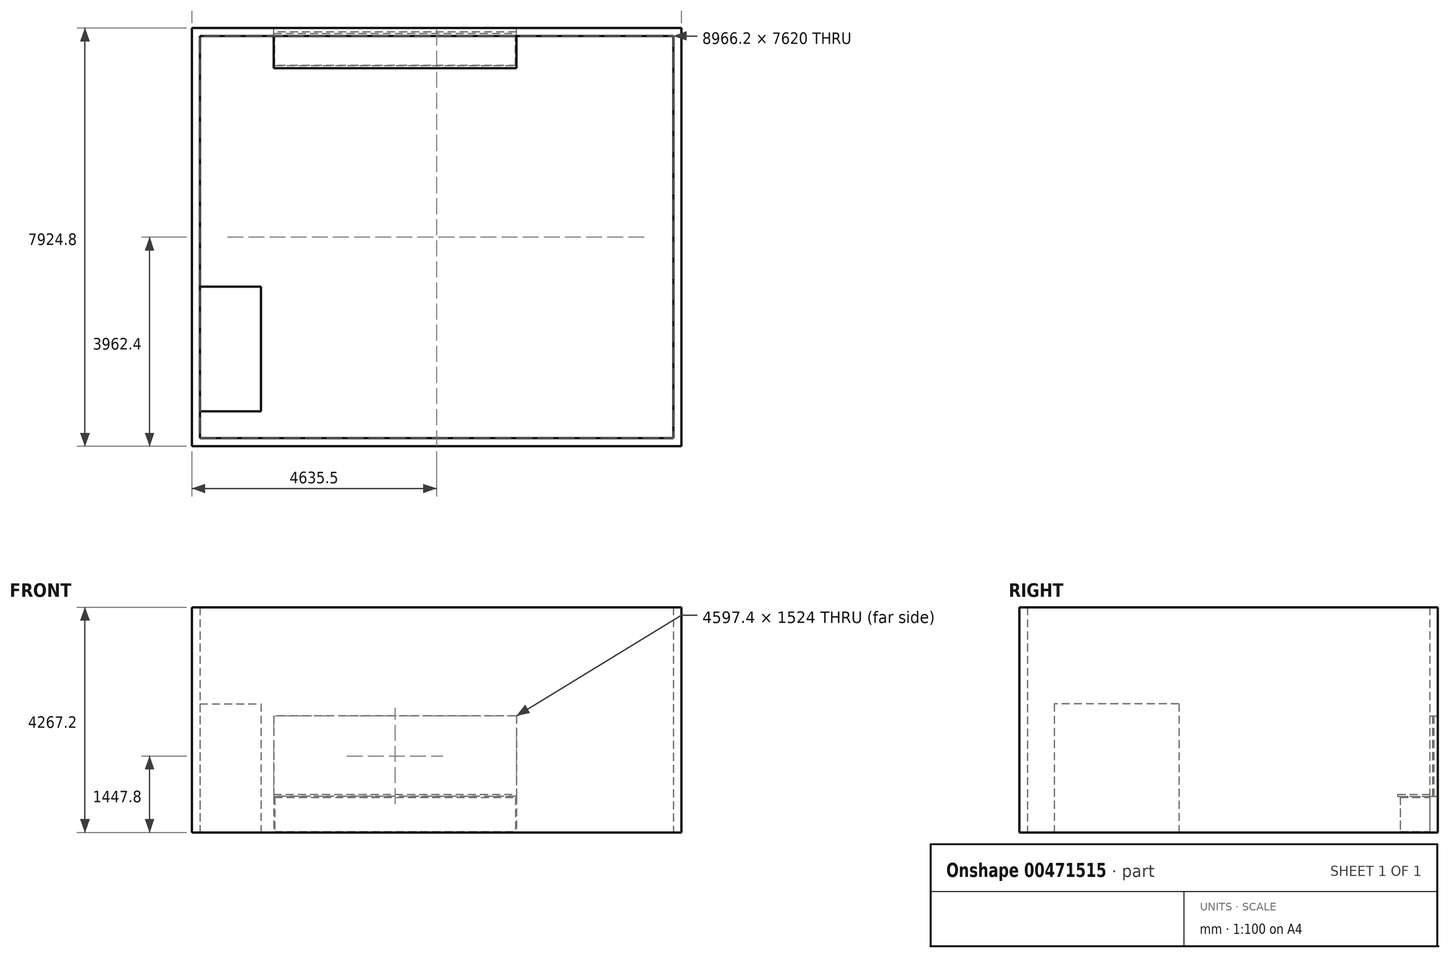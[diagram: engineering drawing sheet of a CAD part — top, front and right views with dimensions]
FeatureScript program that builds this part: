
annotation { "Feature Type Name" : "Feature", "Feature Type Description" : "" }
export const myFeature = defineFeature(function(context is Context, id is Id, definition is map)
    precondition{}
    {
        {
            var Q0;
            Q0=qCreatedBy(makeId("Top.planeOp"),FACE);
            var sketch = newSketch(context, id + "F0", { "sketchPlane" : qUnion([Q0])});
            skLineSegment(sketch, "E0.bottom", {"start": v(4483.1, -3810) * mm, "end": v(-4483.1, -3810) * mm});
            skLineSegment(sketch, "E0.top", {"start": v(4483.1, 3810) * mm, "end": v(-4483.1, 3810) * mm});
            skLineSegment(sketch, "E0.left", {"start": v(4483.1, -3810) * mm, "end": v(4483.1, 3810) * mm});
            skLineSegment(sketch, "E0.right", {"start": v(-4483.1, -3810) * mm, "end": v(-4483.1, 3810) * mm});
            skPoint(sketch, "E0.middle", {"position": v(0, 0) * mm});
            skLineSegment(sketch, "E1.bottom", {"start": v(4483.1, 3810) * mm, "end": v(2247.9, 3810) * mm});
            skLineSegment(sketch, "E1.top", {"start": v(4483.1, 2595.47) * mm, "end": v(2247.9, 2595.47) * mm});
            skLineSegment(sketch, "E1.left", {"start": v(4483.1, 3810) * mm, "end": v(4483.1, 2595.47) * mm});
            skLineSegment(sketch, "E1.right", {"start": v(2247.9, 3810) * mm, "end": v(2247.9, 2595.47) * mm});
            skLineSegment(sketch, "E2.0", {"start": v(4635.5, 3962.4) * mm, "end": v(-4635.5, 3962.4) * mm});
            skLineSegment(sketch, "E2.1", {"start": v(4635.5, -3962.4) * mm, "end": v(4635.5, 3962.4) * mm});
            skLineSegment(sketch, "E2.2", {"start": v(4635.5, -3962.4) * mm, "end": v(-4635.5, -3962.4) * mm});
            skLineSegment(sketch, "E2.3", {"start": v(-4635.5, -3962.4) * mm, "end": v(-4635.5, 3962.4) * mm});
            skLineSegment(sketch, "E3.0", {"start": v(4483.1, 2697.07) * mm, "end": v(2349.5, 2697.07) * mm});
            skLineSegment(sketch, "E3.1", {"start": v(2349.5, 3810) * mm, "end": v(2349.5, 2697.07) * mm});
            skLineSegment(sketch, "E4", {"start": v(2247.9, 3810) * mm, "end": v(2349.5, 3810) * mm});
            skLineSegment(sketch, "E5", {"start": v(4483.1, 2697.07) * mm, "end": v(4483.1, 2595.47) * mm});
            skSolve(sketch);
        }
        {
            var Q0;
            Q0 = qSketchRegion(id + "F0", true);
            extrude(context, id + "F1", {"entities" : qUnion([Q0]), "depth" : 4267.2 * mm});
        }
        {
            var Q0;
            Q0 = qSketchRegion(id + "F0", true);
            extrude(context, id + "F2", {"entities" : qUnion([Q0]), "operationType" : NewBodyOperationType.ADD, "depth" : 25.4 * mm});
        }
        {
            var Q0;
            Q0=sQuery(id+"F0.wireOp",EDGE,"E1.top");
            var Q1;
            Q1=sQuery(id+"F0.wireOp",EDGE,"E3.0");
            var Q2;
            Q2=sQuery(id+"F0.wireOp",EDGE,"E3.1");
            var Q3;
            Q3=sQuery(id+"F0.wireOp",EDGE,"E1.right");
            extrude(context, id + "F3", {"bodyType" : ToolBodyType.SURFACE, "surfaceEntities" : qUnion([Q0, Q1, Q2, Q3]), "depth" : 2438.4 * mm});
        }
        {
            var Q0;
            Q0=makeQuery(id+"F1.opExtrude","SWEPT_FACE",FACE,{"disambiguationData":[OSD([sQuery(id+"F0.wireOp",EDGE,"E2.0")])]});
            var sketch = newSketch(context, id + "F4", { "sketchPlane" : qUnion([Q0])});
            skLineSegment(sketch, "E6.bottom", {"start": v(-1511.3, 2209.8) * mm, "end": v(3086.1, 2209.8) * mm});
            skLineSegment(sketch, "E6.top", {"start": v(-1511.3, 685.8) * mm, "end": v(3086.1, 685.8) * mm});
            skLineSegment(sketch, "E6.left", {"start": v(-1511.3, 2209.8) * mm, "end": v(-1511.3, 685.8) * mm});
            skLineSegment(sketch, "E6.right", {"start": v(3086.1, 2209.8) * mm, "end": v(3086.1, 685.8) * mm});
            skSolve(sketch);
        }
        {
            var Q0;
            Q0 = qSketchRegion(id + "F4", true);
            var Q1;
            Q1=makeQuery(id+"F1.opExtrude","SWEPT_FACE",FACE,{"disambiguationData":[OSD([sQuery(id+"F0.wireOp",EDGE,"E0.top"),sQuery(id+"F0.wireOp",EDGE,"E1.bottom")])]});
            extrude(context, id + "F5", {"entities" : qUnion([Q0]), "operationType" : NewBodyOperationType.REMOVE, "endBound" : BoundingType.UP_TO_SURFACE, "oppositeDirection" : true, "endBoundEntityFace" : qUnion([Q1]), "depth" : 355.6 * mm});
        }
        {
            var Q0;
            Q0=qCreatedBy(makeId("Top.planeOp"),FACE);
            var sketch = newSketch(context, id + "F6", { "sketchPlane" : qUnion([Q0])});
            skLineSegment(sketch, "E7.bottom", {"start": v(-4483.1, -939.8) * mm, "end": v(-3326.74, -939.8) * mm});
            skLineSegment(sketch, "E7.top", {"start": v(-4483.1, -3302.72) * mm, "end": v(-3326.74, -3302.72) * mm});
            skLineSegment(sketch, "E7.left", {"start": v(-4483.1, -939.8) * mm, "end": v(-4483.1, -3302.72) * mm});
            skLineSegment(sketch, "E7.right", {"start": v(-3326.74, -939.8) * mm, "end": v(-3326.74, -3302.72) * mm});
            skLineSegment(sketch, "E8.0", {"start": v(-4483.1, -3150.32) * mm, "end": v(-3479.14, -3150.32) * mm});
            skLineSegment(sketch, "E8.1", {"start": v(-3479.14, -1092.2) * mm, "end": v(-3479.14, -3150.32) * mm});
            skLineSegment(sketch, "E8.2", {"start": v(-4483.1, -1092.2) * mm, "end": v(-3479.14, -1092.2) * mm});
            skSolve(sketch);
        }
        {
            var Q0;
            Q0 = qSketchRegion(id + "F6", true);
            extrude(context, id + "F7", {"entities" : qUnion([Q0]), "operationType" : NewBodyOperationType.ADD, "depth" : 2438.4 * mm});
        }
        {
            var Q0;
            Q0=makeQuery(id+"F1.opExtrude","SWEPT_FACE",FACE,{"disambiguationData":[OSD([sQuery(id+"F0.wireOp",EDGE,"E0.top"),sQuery(id+"F0.wireOp",EDGE,"E1.bottom"),sQuery(id+"F0.wireOp",EDGE,"E4")])]});
            cPlane(context, id + "F8", {"entities" : qUnion([Q0]), "cplaneType" : CPlaneType.OFFSET, "offset" : 76.2 * mm, "oppositeDirection" : true, "width" : 152.4 * mm, "height" : 152.4 * mm});
        }
        {
            var Q0;
            Q0=qCreatedBy(id+"F8.planeOp",FACE);
            var sketch = newSketch(context, id + "F9", { "sketchPlane" : qUnion([Q0])});
            skLineSegment(sketch, "E9.bottom", {"start": v(1511.3, 2209.8) * mm, "end": v(-3086.1, 2209.8) * mm});
            skLineSegment(sketch, "E9.top", {"start": v(1511.3, 685.8) * mm, "end": v(-3086.1, 685.8) * mm});
            skLineSegment(sketch, "E9.left", {"start": v(1511.3, 2209.8) * mm, "end": v(1511.3, 685.8) * mm});
            skLineSegment(sketch, "E9.right", {"start": v(-3086.1, 2209.8) * mm, "end": v(-3086.1, 685.8) * mm});
            skSolve(sketch);
        }
        {
            var Q0;
            Q0 = qSketchRegion(id + "F9", true);
            extrude(context, id + "F10", {"entities" : qUnion([Q0]), "depth" : 25.4 * mm});
        }
        {
            var Q0;
            Q0=makeQuery(id+"F10.opExtrude","CAP_FACE",FACE,{"disambiguationData":[OSD([sQuery(id+"F9.wireOp",EDGE,"E9.bottom"),sQuery(id+"F9.wireOp",EDGE,"E9.top"),sQuery(id+"F9.wireOp",EDGE,"E9.left"),sQuery(id+"F9.wireOp",EDGE,"E9.right")])],"isStart":false});
            var sketch = newSketch(context, id + "F11", { "sketchPlane" : qUnion([Q0])});
            skLineSegment(sketch, "E10.bottom", {"start": v(-3086.1, 723.9) * mm, "end": v(1511.3, 723.9) * mm});
            skLineSegment(sketch, "E10.top", {"start": v(-3086.1, 685.8) * mm, "end": v(1511.3, 685.8) * mm});
            skLineSegment(sketch, "E10.left", {"start": v(-3086.1, 723.9) * mm, "end": v(-3086.1, 685.8) * mm});
            skLineSegment(sketch, "E10.right", {"start": v(1511.3, 723.9) * mm, "end": v(1511.3, 685.8) * mm});
            skSolve(sketch);
        }
        {
            var Q0;
            Q0=makeQuery(id+"F1.opExtrude","SWEPT_FACE",FACE,{"disambiguationData":[OSD([sQuery(id+"F0.wireOp",EDGE,"E0.top"),sQuery(id+"F0.wireOp",EDGE,"E1.bottom"),sQuery(id+"F0.wireOp",EDGE,"E4")])]});
            var sketch = newSketch(context, id + "F12", { "sketchPlane" : qUnion([Q0])});
            skLineSegment(sketch, "E11.bottom", {"start": v(-3086.1, 685.8) * mm, "end": v(1511.3, 685.8) * mm});
            skLineSegment(sketch, "E11.top", {"start": v(-3086.1, 0) * mm, "end": v(1511.3, 0) * mm});
            skLineSegment(sketch, "E11.left", {"start": v(-3086.1, 685.8) * mm, "end": v(-3086.1, 0) * mm});
            skLineSegment(sketch, "E11.right", {"start": v(1511.3, 685.8) * mm, "end": v(1511.3, 0) * mm});
            skLineSegment(sketch, "E12.0", {"start": v(-3067.05, 666.75) * mm, "end": v(1492.25, 666.75) * mm});
            skLineSegment(sketch, "E12.1", {"start": v(-3067.05, 666.75) * mm, "end": v(-3067.05, 19.05) * mm});
            skLineSegment(sketch, "E12.2", {"start": v(-3067.05, 19.05) * mm, "end": v(1492.25, 19.05) * mm});
            skLineSegment(sketch, "E12.3", {"start": v(1492.25, 666.75) * mm, "end": v(1492.25, 19.05) * mm});
            skSolve(sketch);
        }
        {
            var Q0;
            Q0 = qSketchRegion(id + "F12", true);
            extrude(context, id + "F13", {"entities" : qUnion([Q0]), "depth" : 558.8 * mm});
        }
        {
            var Q0;
            Q0 = qSketchRegion(id + "F11", true);
            extrude(context, id + "F14", {"entities" : qUnion([Q0]), "depth" : 660.4 * mm});
        }
        {
            var Q0;
            Q0=makeQuery(id+"F1.opExtrude","SWEPT_FACE",FACE,{"disambiguationData":[OSD([sQuery(id+"F0.wireOp",EDGE,"E0.right")])]});
            var sketch = newSketch(context, id + "F15", { "sketchPlane" : qUnion([Q0])});
            skLineSegment(sketch, "E13.bottom", {"start": v(-939.8, 3302) * mm, "end": v(-889, 3302) * mm});
            skLineSegment(sketch, "E13.top", {"start": v(-939.8, 3251.2) * mm, "end": v(-889, 3251.2) * mm});
            skLineSegment(sketch, "E13.left", {"start": v(-939.8, 3302) * mm, "end": v(-939.8, 3251.2) * mm});
            skLineSegment(sketch, "E13.right", {"start": v(-889, 3302) * mm, "end": v(-889, 3251.2) * mm});
            skSolve(sketch);
        }
        {
            var Q0;
            Q0 = qSketchRegion(id + "F15", true);
            extrude(context, id + "F16", {"entities" : qUnion([Q0]), "endBound" : BoundingType.UP_TO_NEXT, "depth" : 25.4 * mm});
        }
        {
            var Q0;
            Q0=makeQuery(id+"F16.opExtrude","SWEPT_BODY",BODY,{"disambiguationData":[OSD([sQuery(id+"F15.wireOp",EDGE,"E13.bottom"),sQuery(id+"F15.wireOp",EDGE,"E13.top"),sQuery(id+"F15.wireOp",EDGE,"E13.left"),sQuery(id+"F15.wireOp",EDGE,"E13.right")])]});
            deleteBodies(context, id + "F17", {"entities" : qUnion([Q0])});
        }
        {
            var Q0;
            Q0=makeQuery(id+"F7.opExtrude","SWEPT_FACE",FACE,{"disambiguationData":[OSD([sQuery(id+"F6.wireOp",EDGE,"E7.bottom")])]});
            cPlane(context, id + "F18", {"entities" : qUnion([Q0]), "cplaneType" : CPlaneType.OFFSET, "offset" : 25.4 * mm, "width" : 152.4 * mm, "height" : 152.4 * mm});
        }
    });
